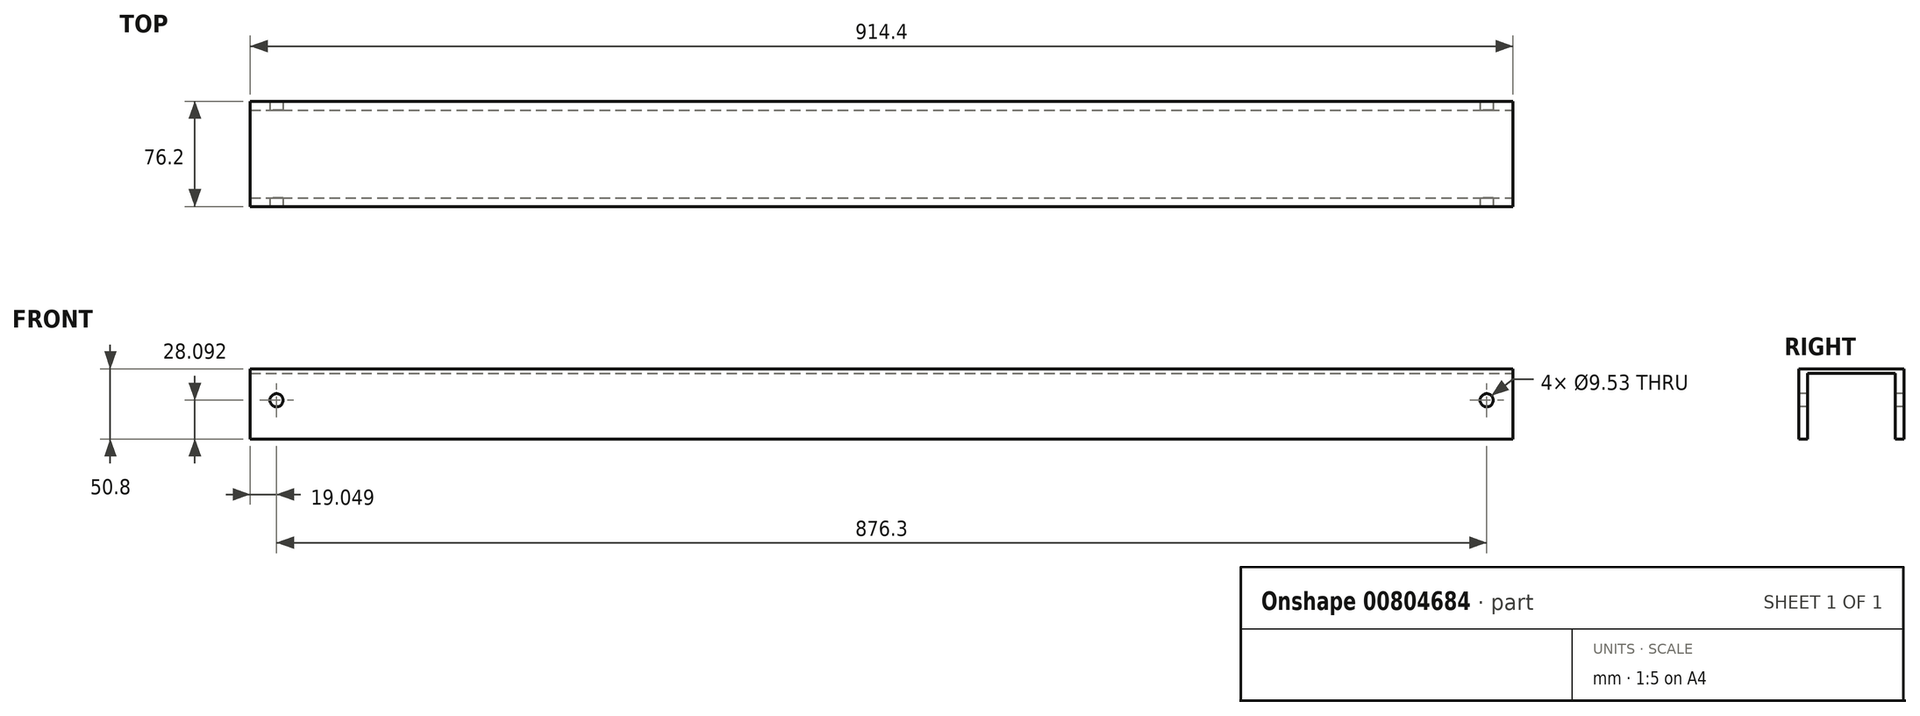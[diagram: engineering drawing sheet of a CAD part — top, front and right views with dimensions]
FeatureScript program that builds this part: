
annotation { "Feature Type Name" : "Feature", "Feature Type Description" : "" }
export const myFeature = defineFeature(function(context is Context, id is Id, definition is map)
    precondition{}
    {
        {
            var Q0;
            Q0=qCreatedBy(makeId("Front.planeOp"),FACE);
            var sketch = newSketch(context, id + "F0", { "sketchPlane" : qUnion([Q0])});
            skLineSegment(sketch, "E0", {"start": v(0, 0) * mm, "end": v(107.49, 609.6) * mm, "construction": true});
            skLineSegment(sketch, "E1", {"start": v(107.49, 609.6) * mm, "end": v(157.52, 600.78) * mm, "construction": true});
            skLineSegment(sketch, "E2", {"start": v(157.52, 600.78) * mm, "end": v(51.58, 0) * mm, "construction": true});
            skLineSegment(sketch, "E3", {"start": v(51.58, 0) * mm, "end": v(0, 0) * mm, "construction": true});
            skLineSegment(sketch, "E4", {"start": v(1077.8, 0) * mm, "end": v(971.86, 600.78) * mm, "construction": true});
            skLineSegment(sketch, "E5", {"start": v(971.86, 600.78) * mm, "end": v(1021.89, 609.6) * mm, "construction": true});
            skLineSegment(sketch, "E6", {"start": v(1021.89, 609.6) * mm, "end": v(1129.38, 0) * mm, "construction": true});
            skLineSegment(sketch, "E7", {"start": v(1129.38, 0) * mm, "end": v(1077.8, 0) * mm, "construction": true});
            skLineSegment(sketch, "E8.bottom", {"start": v(107.49, 609.6) * mm, "end": v(1021.89, 609.6) * mm});
            skLineSegment(sketch, "E8.top", {"start": v(107.49, 558.8) * mm, "end": v(1021.89, 558.8) * mm});
            skLineSegment(sketch, "E8.left", {"start": v(107.49, 609.6) * mm, "end": v(107.49, 558.8) * mm});
            skLineSegment(sketch, "E8.right", {"start": v(1021.89, 609.6) * mm, "end": v(1021.89, 558.8) * mm});
            skSolve(sketch);
        }
        {
            var Q0;
            Q0=makeQuery(id+"F0.imprint","IMPRINT",FACE,{"disambiguationData":[TD([[makeQuery(id+"F0.imprint","IMPRINT",EDGE,{"derivedFrom":sQuery(id+"F0.wireOp",EDGE,"E8.bottom")}),-1.0]])]});
            extrude(context, id + "F1", {"entities" : qUnion([Q0]), "depth" : 6.35 * mm, "offsetDistance" : 25.4 * mm});
        }
        {
            var Q0;
            Q0=makeQuery(id+"F1.opExtrude","SWEPT_FACE",FACE,{"disambiguationData":[OSD([sQuery(id+"F0.wireOp",EDGE,"E8.bottom")])]});
            var sketch = newSketch(context, id + "F2", { "sketchPlane" : qUnion([Q0])});
            skLineSegment(sketch, "E9.bottom", {"start": v(107.49, -6.35) * mm, "end": v(1021.89, -6.35) * mm});
            skLineSegment(sketch, "E9.top", {"start": v(107.49, 69.85) * mm, "end": v(1021.89, 69.85) * mm});
            skLineSegment(sketch, "E9.left", {"start": v(107.49, -6.35) * mm, "end": v(107.49, 69.85) * mm});
            skLineSegment(sketch, "E9.right", {"start": v(1021.89, -6.35) * mm, "end": v(1021.89, 69.85) * mm});
            skSolve(sketch);
        }
        {
            var Q0;
            {var subQ0=sQuery(id+"F2.wireOp",EDGE,"E9.top");Q0=makeQuery(id+"F2.imprint","IMPRINT",FACE,{"disambiguationData":[TD([[makeQuery(id+"F2.imprint","IMPRINT",EDGE,{"derivedFrom":subQ0}),-1.0]])]});}
            extrude(context, id + "F3", {"entities" : qUnion([Q0]), "operationType" : NewBodyOperationType.ADD, "oppositeDirection" : true, "depth" : 3.17 * mm, "offsetDistance" : 25.4 * mm});
        }
        {
            var Q0;
            Q0=makeQuery(id+"F3.opExtrude","CAP_FACE",FACE,{"disambiguationData":[OSD([sQuery(id+"F0.wireOp",EDGE,"E8.bottom"),sQuery(id+"F2.wireOp",EDGE,"E9.top"),sQuery(id+"F2.wireOp",EDGE,"E9.left"),sQuery(id+"F2.wireOp",EDGE,"E9.right")])],"isStart":false});
            var sketch = newSketch(context, id + "F4", { "sketchPlane" : qUnion([Q0])});
            skLineSegment(sketch, "E10.bottom", {"start": v(107.49, -69.85) * mm, "end": v(1021.89, -69.85) * mm});
            skLineSegment(sketch, "E10.top", {"start": v(107.49, -63.5) * mm, "end": v(1021.89, -63.5) * mm});
            skLineSegment(sketch, "E10.left", {"start": v(107.49, -69.85) * mm, "end": v(107.49, -63.5) * mm});
            skLineSegment(sketch, "E10.right", {"start": v(1021.89, -69.85) * mm, "end": v(1021.89, -63.5) * mm});
            skSolve(sketch);
        }
        {
            var Q0;
            Q0=makeQuery(id+"F4.imprint","IMPRINT",FACE,{"disambiguationData":[TD([[makeQuery(id+"F4.imprint","IMPRINT",EDGE,{"derivedFrom":sQuery(id+"F4.wireOp",EDGE,"E10.bottom")}),1.0]])]});
            var Q1;
            Q1=makeQuery(id+"F1.opExtrude","SWEPT_FACE",FACE,{"disambiguationData":[OSD([sQuery(id+"F0.wireOp",EDGE,"E8.top")])]});
            extrude(context, id + "F5", {"entities" : qUnion([Q0]), "operationType" : NewBodyOperationType.ADD, "endBound" : BoundingType.UP_TO_SURFACE, "depth" : 25.4 * mm, "endBoundEntityFace" : qUnion([Q1]), "offsetDistance" : 25.4 * mm});
        }
        {
            var Q0;
            Q0=makeQuery(id+"F1.opExtrude","CAP_FACE",FACE,{"disambiguationData":[OSD([sQuery(id+"F0.wireOp",EDGE,"E8.bottom"),sQuery(id+"F0.wireOp",EDGE,"E8.top"),sQuery(id+"F0.wireOp",EDGE,"E8.left"),sQuery(id+"F0.wireOp",EDGE,"E8.right")])],"isStart":false});
            var sketch = newSketch(context, id + "F6", { "sketchPlane" : qUnion([Q0])});
            skPoint(sketch, "E11", {"position": v(126.54, 586.9) * mm});
            skPoint(sketch, "E12", {"position": v(1002.84, 586.9) * mm});
            skSolve(sketch);
        }
        {
            var Q0;
            Q0=sQuery(id+"F6.wireOp",VERTEX,"E11");
            var Q1;
            Q1=sQuery(id+"F6.wireOp",VERTEX,"E12");
            var Q2;
            Q2=makeQuery(id+"F1.opExtrude","SWEPT_BODY",BODY,{"disambiguationData":[OSD([sQuery(id+"F0.wireOp",EDGE,"E8.bottom"),sQuery(id+"F0.wireOp",EDGE,"E8.top"),sQuery(id+"F0.wireOp",EDGE,"E8.left"),sQuery(id+"F0.wireOp",EDGE,"E8.right")])]});
            hole(context, id + "F7", {"style" : HoleStyle.SIMPLE, "endStyle" : HoleEndStyle.THROUGH, "holeDiameter" : 9.52 * mm, "majorDiameter" : 6.35 * mm, "isTappedThrough" : true, "tappedDepth" : 12.7 * mm, "tapClearance" : 3, "locations" : qUnion([Q0, Q1]), "scope" : qUnion([Q2])});
        }
    });
